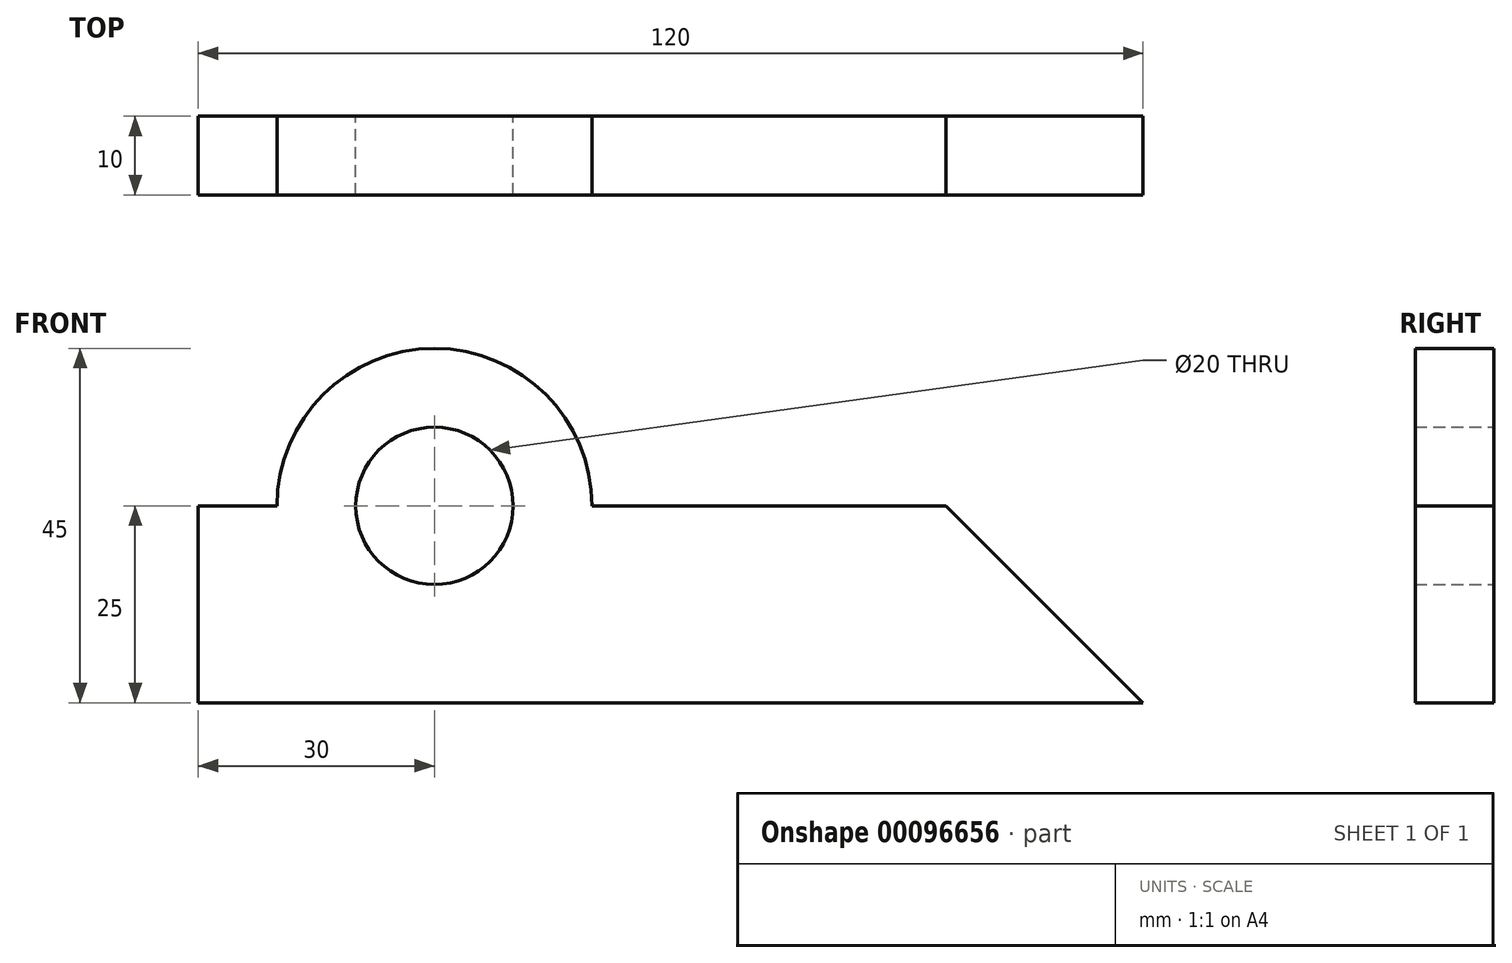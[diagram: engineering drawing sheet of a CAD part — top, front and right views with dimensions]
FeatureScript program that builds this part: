
annotation { "Feature Type Name" : "Feature", "Feature Type Description" : "" }
export const myFeature = defineFeature(function(context is Context, id is Id, definition is map)
    precondition{}
    {
        {
            var Q0;
            Q0=qCreatedBy(makeId("Front.planeOp"),FACE);
            var sketch = newSketch(context, id + "F0", { "sketchPlane" : qUnion([Q0])});
            skLineSegment(sketch, "E0", {"start": v(0, 0) * mm, "end": v(0, 25) * mm});
            skLineSegment(sketch, "E1", {"start": v(0, 0) * mm, "end": v(120, 0) * mm});
            skLineSegment(sketch, "E2", {"start": v(120, 0) * mm, "end": v(95, 25) * mm});
            skLineSegment(sketch, "E3", {"start": v(0, 25) * mm, "end": v(10, 25) * mm});
            skLineSegment(sketch, "E4", {"start": v(50, 25) * mm, "end": v(95, 25) * mm});
            skLineSegment(sketch, "E5", {"start": v(30, 32.85) * mm, "end": v(30, 15.57) * mm, "construction": true});
            skLineSegment(sketch, "E6", {"start": v(10, 25) * mm, "end": v(50, 25) * mm, "construction": true});
            skCircle(sketch, "E7", {"center": v(30, 25) * mm, "radius": 10 * mm});
            skArc(sketch, "E8", {"start": v(10, 25) * mm, "mid": v(30, 45) * mm, "end": v(50, 25) * mm});
            skSolve(sketch);
        }
        {
            var Q0;
            Q0 = qSketchRegion(id + "F0", true);
            extrude(context, id + "F1", {"entities" : qUnion([Q0]), "depth" : 10 * mm});
        }
    });
